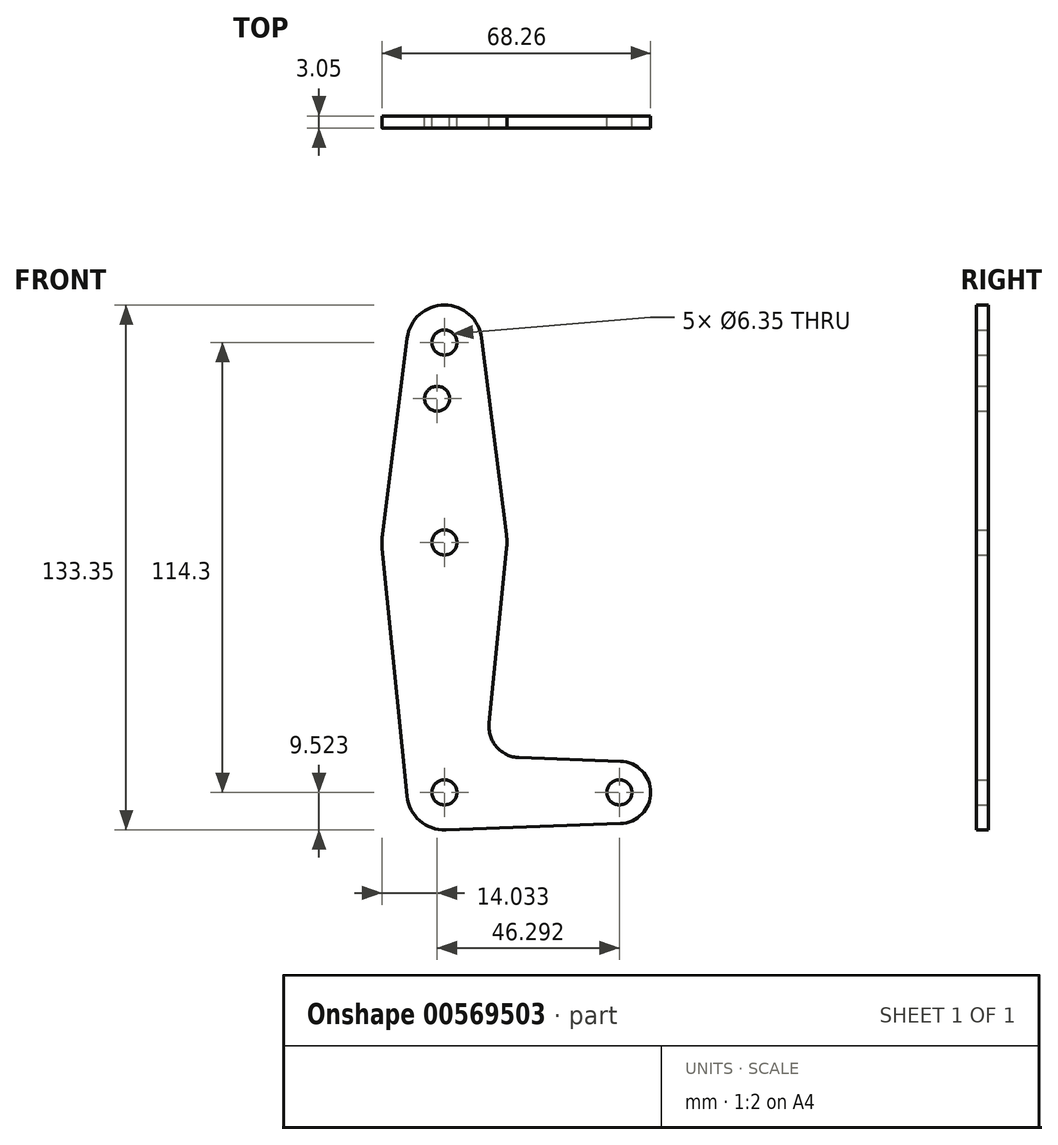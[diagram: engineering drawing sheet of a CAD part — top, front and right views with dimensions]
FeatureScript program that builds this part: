
annotation { "Feature Type Name" : "Feature", "Feature Type Description" : "" }
export const myFeature = defineFeature(function(context is Context, id is Id, definition is map)
    precondition{}
    {
        {
            var Q0;
            Q0=qCreatedBy(makeId("Front.planeOp"),FACE);
            var sketch = newSketch(context, id + "F0", { "sketchPlane" : qUnion([Q0])});
            skLineSegment(sketch, "E0", {"start": v(-12.16, 66.4) * mm, "end": v(-12.16, -47.9) * mm, "construction": true});
            skLineSegment(sketch, "E1", {"start": v(-12.16, -47.9) * mm, "end": v(32.3, -47.9) * mm, "construction": true});
            skCircle(sketch, "E2", {"center": v(-12.16, 66.4) * mm, "radius": 9.52 * mm});
            skLineSegment(sketch, "E3", {"start": v(-12.16, -47.9) * mm, "end": v(-12.16, 15.6) * mm});
            skCircle(sketch, "E4", {"center": v(-12.16, 15.6) * mm, "radius": 15.88 * mm});
            skCircle(sketch, "E5", {"center": v(-12.16, -47.9) * mm, "radius": 9.52 * mm});
            skCircle(sketch, "E6", {"center": v(32.3, -47.9) * mm, "radius": 7.93 * mm});
            skLineSegment(sketch, "E7", {"start": v(-21.6, 67.6) * mm, "end": v(-27.9, 17.59) * mm});
            skLineSegment(sketch, "E8", {"start": v(-2.7, 67.6) * mm, "end": v(3.6, 17.59) * mm});
            skLineSegment(sketch, "E9", {"start": v(32.58, -55.82) * mm, "end": v(-11.81, -57.42) * mm});
            skCircle(sketch, "E10", {"center": v(-12.16, 66.4) * mm, "radius": 3.18 * mm});
            skCircle(sketch, "E11", {"center": v(-12.16, 15.6) * mm, "radius": 3.18 * mm});
            skCircle(sketch, "E12", {"center": v(-12.16, -47.9) * mm, "radius": 3.18 * mm});
            skCircle(sketch, "E13", {"center": v(32.3, -47.9) * mm, "radius": 3.18 * mm});
            skCircle(sketch, "E14", {"center": v(-14, 52.13) * mm, "radius": 3.18 * mm});
            skLineSegment(sketch, "E15", {"start": v(-27.95, 14.02) * mm, "end": v(-21.63, -48.85) * mm});
            skLineSegment(sketch, "E16", {"start": v(3.64, 14.02) * mm, "end": v(-0.82, -30.3) * mm});
            skLineSegment(sketch, "E17", {"start": v(6.81, -39.05) * mm, "end": v(32.58, -39.97) * mm});
            skArc(sketch, "E18.filletArc", {"start": v(-0.82, -30.3) * mm, "mid": v(1.1, -36.33) * mm, "end": v(6.81, -39.05) * mm});
            skSolve(sketch);
        }
        {
            var Q0;
            Q0 = qSketchRegion(id + "F0", true);
            extrude(context, id + "F1", {"entities" : qUnion([Q0]), "depth" : 3.05 * mm, "offsetDistance" : 25.4 * mm});
        }
    });
